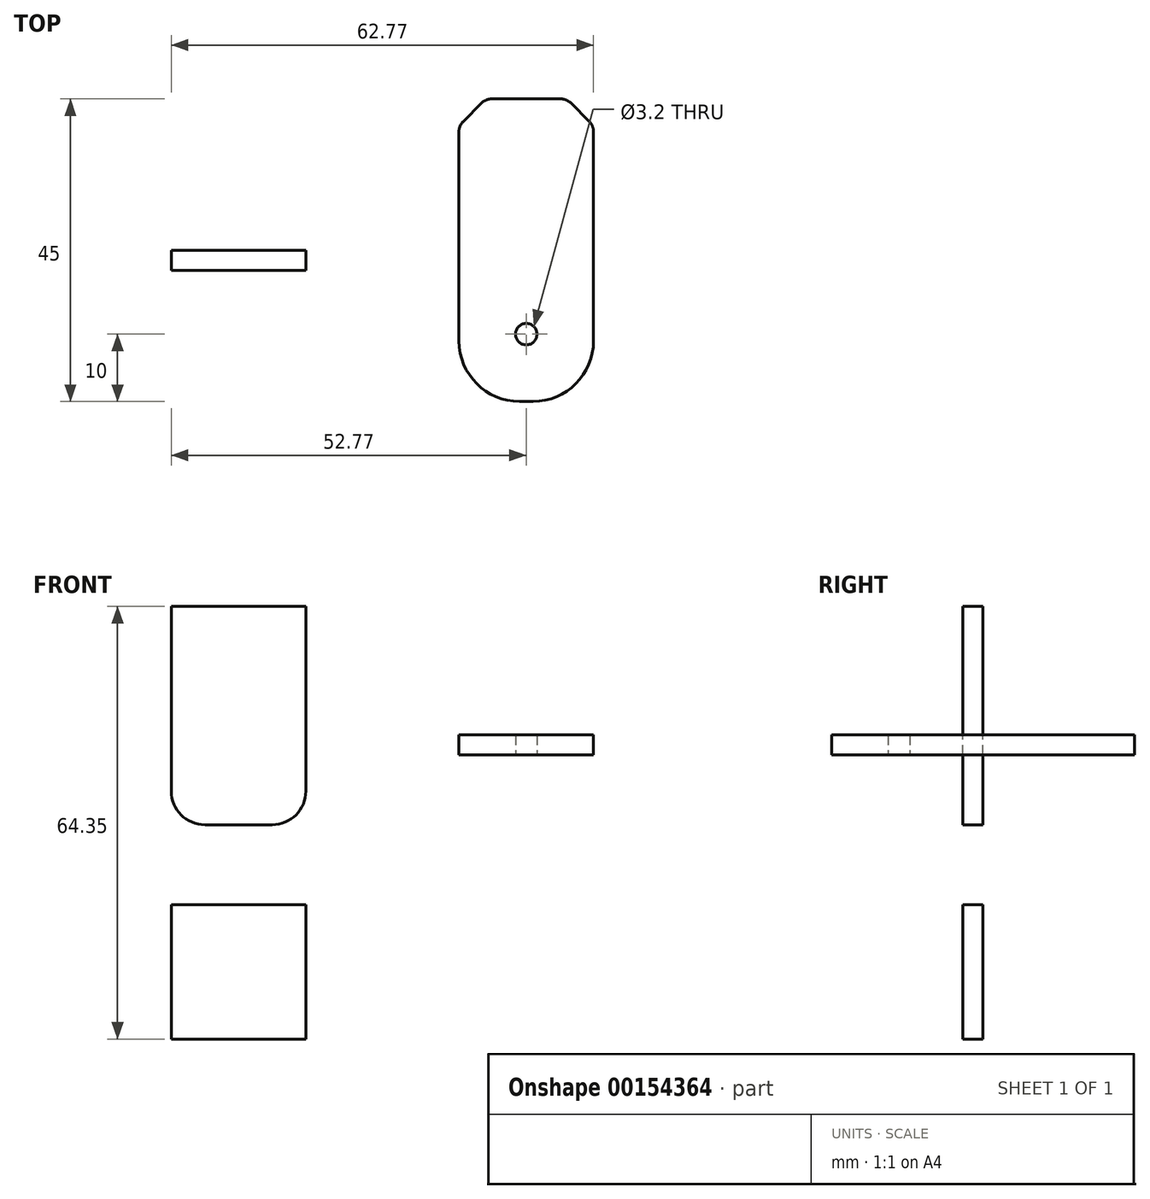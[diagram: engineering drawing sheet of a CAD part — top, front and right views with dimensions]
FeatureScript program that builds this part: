
annotation { "Feature Type Name" : "Feature", "Feature Type Description" : "" }
export const myFeature = defineFeature(function(context is Context, id is Id, definition is map)
    precondition{}
    {
        {
            var Q0;
            Q0=qCreatedBy(makeId("Top.planeOp"),FACE);
            var sketch = newSketch(context, id + "F0", { "sketchPlane" : qUnion([Q0])});
            skLineSegment(sketch, "E0.bottom", {"start": v(10, 22.5) * mm, "end": v(-10, 22.5) * mm});
            skLineSegment(sketch, "E0.top", {"start": v(10, -22.5) * mm, "end": v(-10, -22.5) * mm});
            skLineSegment(sketch, "E0.left", {"start": v(10, 22.5) * mm, "end": v(10, -22.5) * mm});
            skLineSegment(sketch, "E0.right", {"start": v(-10, 22.5) * mm, "end": v(-10, -22.5) * mm});
            skPoint(sketch, "E0.middle", {"position": v(0, 0) * mm});
            skCircle(sketch, "E1", {"center": v(0, -12.5) * mm, "radius": 1.6 * mm});
            skCircle(sketch, "E2", {"center": v(0, -12.5) * mm, "radius": 10 * mm, "construction": true});
            skSolve(sketch);
        }
        {
            var Q0;
            Q0 = qSketchRegion(id + "F0", true);
            extrude(context, id + "F1", {"entities" : qUnion([Q0]), "depth" : 3 * mm});
        }
        {
            var Q0;
            Q0=makeQuery(id+"F1.opExtrude","SWEPT_EDGE",EDGE,{"disambiguationData":[OSD([sQuery(id+"F0.wireOp",EDGE,"E0.top"),sQuery(id+"F0.wireOp",EDGE,"E0.left")])]});
            var Q1;
            Q1=makeQuery(id+"F1.opExtrude","SWEPT_EDGE",EDGE,{"disambiguationData":[OSD([sQuery(id+"F0.wireOp",EDGE,"E0.top"),sQuery(id+"F0.wireOp",EDGE,"E0.right")])]});
            fillet(context, id + "F2", {"entities" : qUnion([Q0, Q1]), "radius" : 9 * mm, "tangentPropagation" : true, "allowEdgeOverflow" : false});
        }
        {
            var Q0;
            Q0=makeQuery(id+"F1.opExtrude","SWEPT_EDGE",EDGE,{"disambiguationData":[OSD([sQuery(id+"F0.wireOp",EDGE,"E0.bottom"),sQuery(id+"F0.wireOp",EDGE,"E0.right")])]});
            var Q1;
            Q1=makeQuery(id+"F1.opExtrude","SWEPT_EDGE",EDGE,{"disambiguationData":[OSD([sQuery(id+"F0.wireOp",EDGE,"E0.bottom"),sQuery(id+"F0.wireOp",EDGE,"E0.left")])]});
            chamfer(context, id + "F3", {"entities" : qUnion([Q0, Q1]), "width" : 4 * mm, "tangentPropagation" : true});
        }
        {
            var Q0;
            {var subQ0=sQuery(id+"F0.wireOp",EDGE,"E0.bottom");Q0=makeQuery(id+"F3.opChamfer","BLEND_EDGE",EDGE,{"blendedFrom":[makeQuery(id+"F1.opExtrude","SWEPT_EDGE",EDGE,{"disambiguationData":[OSD([subQ0,sQuery(id+"F0.wireOp",EDGE,"E0.right")])]}),makeQuery(id+"F1.opExtrude","SWEPT_FACE",FACE,{"disambiguationData":[OSD([subQ0])]})],"blendedInto":[makeQuery(id+"F1.opExtrude","SWEPT_FACE",FACE,{"disambiguationData":[OSD([subQ0])]})]});}
            var Q1;
            {var subQ0=sQuery(id+"F0.wireOp",EDGE,"E0.bottom");Q1=makeQuery(id+"F3.opChamfer","BLEND_EDGE",EDGE,{"blendedFrom":[makeQuery(id+"F1.opExtrude","SWEPT_EDGE",EDGE,{"disambiguationData":[OSD([subQ0,sQuery(id+"F0.wireOp",EDGE,"E0.left")])]}),makeQuery(id+"F1.opExtrude","SWEPT_FACE",FACE,{"disambiguationData":[OSD([subQ0])]})],"blendedInto":[makeQuery(id+"F1.opExtrude","SWEPT_FACE",FACE,{"disambiguationData":[OSD([subQ0])]})]});}
            var Q2;
            {var subQ0=sQuery(id+"F0.wireOp",EDGE,"E0.left");Q2=makeQuery(id+"F3.opChamfer","BLEND_EDGE",EDGE,{"blendedFrom":[makeQuery(id+"F1.opExtrude","SWEPT_EDGE",EDGE,{"disambiguationData":[OSD([sQuery(id+"F0.wireOp",EDGE,"E0.bottom"),subQ0])]}),makeQuery(id+"F1.opExtrude","SWEPT_FACE",FACE,{"disambiguationData":[OSD([subQ0])]})],"blendedInto":[makeQuery(id+"F1.opExtrude","SWEPT_FACE",FACE,{"disambiguationData":[OSD([subQ0])]})]});}
            var Q3;
            {var subQ0=sQuery(id+"F0.wireOp",EDGE,"E0.right");Q3=makeQuery(id+"F3.opChamfer","BLEND_EDGE",EDGE,{"blendedFrom":[makeQuery(id+"F1.opExtrude","SWEPT_EDGE",EDGE,{"disambiguationData":[OSD([sQuery(id+"F0.wireOp",EDGE,"E0.bottom"),subQ0])]}),makeQuery(id+"F1.opExtrude","SWEPT_FACE",FACE,{"disambiguationData":[OSD([subQ0])]})],"blendedInto":[makeQuery(id+"F1.opExtrude","SWEPT_FACE",FACE,{"disambiguationData":[OSD([subQ0])]})]});}
            fillet(context, id + "F4", {"entities" : qUnion([Q0, Q1, Q2, Q3]), "radius" : 2 * mm, "tangentPropagation" : true, "allowEdgeOverflow" : false});
        }
        {
            var Q0;
            Q0=qCreatedBy(makeId("Front.planeOp"),FACE);
            var sketch = newSketch(context, id + "F5", { "sketchPlane" : qUnion([Q0])});
            skLineSegment(sketch, "E3.bottom", {"start": v(-32.77, -42.25) * mm, "end": v(-52.77, -42.25) * mm});
            skLineSegment(sketch, "E3.top", {"start": v(-32.77, -22.25) * mm, "end": v(-52.77, -22.25) * mm});
            skLineSegment(sketch, "E3.left", {"start": v(-32.77, -42.25) * mm, "end": v(-32.77, -22.25) * mm});
            skLineSegment(sketch, "E3.right", {"start": v(-52.77, -42.25) * mm, "end": v(-52.77, -22.25) * mm});
            skPoint(sketch, "E3.middle", {"position": v(-42.77, -32.25) * mm});
            skLineSegment(sketch, "E4.bottom", {"start": v(-52.77, -10.37) * mm, "end": v(-32.77, -10.37) * mm});
            skLineSegment(sketch, "E4.top", {"start": v(-52.77, 22.1) * mm, "end": v(-32.77, 22.1) * mm});
            skLineSegment(sketch, "E4.left", {"start": v(-52.77, -10.37) * mm, "end": v(-52.77, 22.1) * mm});
            skLineSegment(sketch, "E4.right", {"start": v(-32.77, -10.37) * mm, "end": v(-32.77, 22.1) * mm});
            skSolve(sketch);
        }
        {
            var Q0;
            Q0 = qSketchRegion(id + "F5", true);
            extrude(context, id + "F6", {"entities" : qUnion([Q0]), "depth" : 3 * mm});
        }
        {
            var Q0;
            Q0=makeQuery(id+"F6.opExtrude","SWEPT_EDGE",EDGE,{"disambiguationData":[OSD([sQuery(id+"F5.wireOp",EDGE,"E4.bottom"),sQuery(id+"F5.wireOp",EDGE,"E4.right")])]});
            var Q1;
            Q1=makeQuery(id+"F6.opExtrude","SWEPT_EDGE",EDGE,{"disambiguationData":[OSD([sQuery(id+"F5.wireOp",EDGE,"E4.bottom"),sQuery(id+"F5.wireOp",EDGE,"E4.left")])]});
            fillet(context, id + "F7", {"entities" : qUnion([Q0, Q1]), "radius" : 5 * mm, "tangentPropagation" : true, "allowEdgeOverflow" : false});
        }
    });
